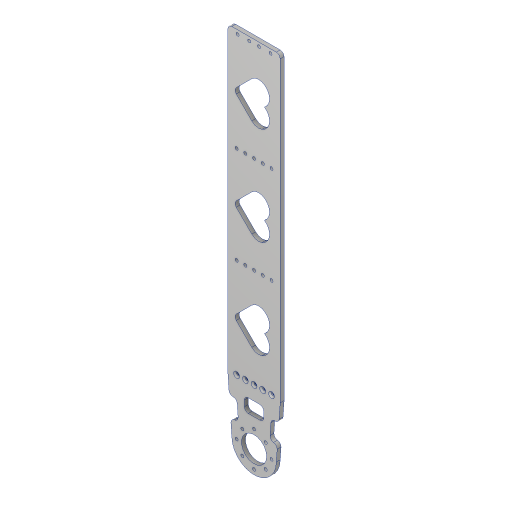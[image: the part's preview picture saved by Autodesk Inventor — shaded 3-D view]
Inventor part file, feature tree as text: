
AUTODESK INVENTOR PART (.ipt)
format: ipt  version: 2023.2 (Build 272271000, 271)  size: 679,936 bytes
history: native  units: mm
features: extrude x17, sketch x15, projected_geometry x11, fillet x8, other x1, chamfer x1
ambient origin geometry x8: Origin, YZ Plane, XZ Plane, XY Plane, X Axis, Y Axis, Z Axis, Center Point
bodies: Body1 (feature_tree)
feature tree (53):
  other  "솔리드1"
  extrude  "돌출1"  Depth=26.0mm
  extrude  "돌출2"  Depth=46.0mm
  extrude  "돌출3"  Depth=54.0mm
  extrude  "돌출4"  Depth=62.0mm
  fillet  "모깎기1"  Radius=27.0mm
  extrude  "돌출6"  TaperAngle=0.0deg  [1 undecoded]
  fillet  "모깎기3"  Radius=7.0mm
  extrude  "돌출7"  TaperAngle=90.0deg  [1 undecoded]
  fillet  "모깎기4"  Radius=7.0mm
  extrude  "돌출8"  TaperAngle=90.0deg  [1 undecoded]
  extrude  "돌출9"  Depth=4.0mm TaperAngle=0.0deg
  fillet  "모깎기5"  Radius=26.0mm
  extrude  "돌출10"  Depth=4.0mm TaperAngle=0.0deg
  sketch  "스케치12"
  extrude  "돌출11"  Depth=3.2mm
  extrude  "돌출12"  Depth=4.0mm TaperAngle=0.0deg
  extrude  "돌출13"  Depth=3.2mm
  fillet  "모깎기6"  Radius=4.5mm
  sketch  "스케치14"
  extrude  "돌출15"  Depth=3.2mm
  extrude  "돌출16"  Depth=3.2mm
  extrude  "돌출17"  Depth=3.2mm
  extrude  "돌출18"  Depth=3.2mm
  chamfer  "모따기2"  Distance=4.5mm
  fillet  "모깎기7"  Radius=4.5mm
  extrude  "돌출20"  Depth=4.5mm
  fillet  "모깎기9"  Radius=4.5mm
  fillet  "모깎기10"  Radius=9.0mm
  sketch  "스케치1"
  sketch  "스케치2"
  sketch  "스케치3"
  sketch  "스케치4"
  projected_geometry  "투영된 루프1"
  sketch  "스케치7"
  projected_geometry  "투영된 루프3"
  sketch  "스케치8"
  sketch  "스케치9"
  projected_geometry  "투영된 루프4"
  sketch  "스케치10"
  projected_geometry  "투영된 루프5"
  sketch  "스케치11"
  projected_geometry  "투영된 루프6"
  projected_geometry  "투영된 루프7"
  sketch  "스케치13"
  projected_geometry  "투영된 루프8"
  projected_geometry  "투영된 루프9"
  sketch  "스케치15"
  projected_geometry  "투영된 루프10"
  sketch  "스케치16"
  projected_geometry  "투영된 루프11"
  sketch  "스케치19"
  projected_geometry  "투영된 루프14"
note: 3 required parameter values undecoded (feature->parameter linkage not recoverable at this tier; creation-order binding heuristic only, values carry confidence <= 0.55)
